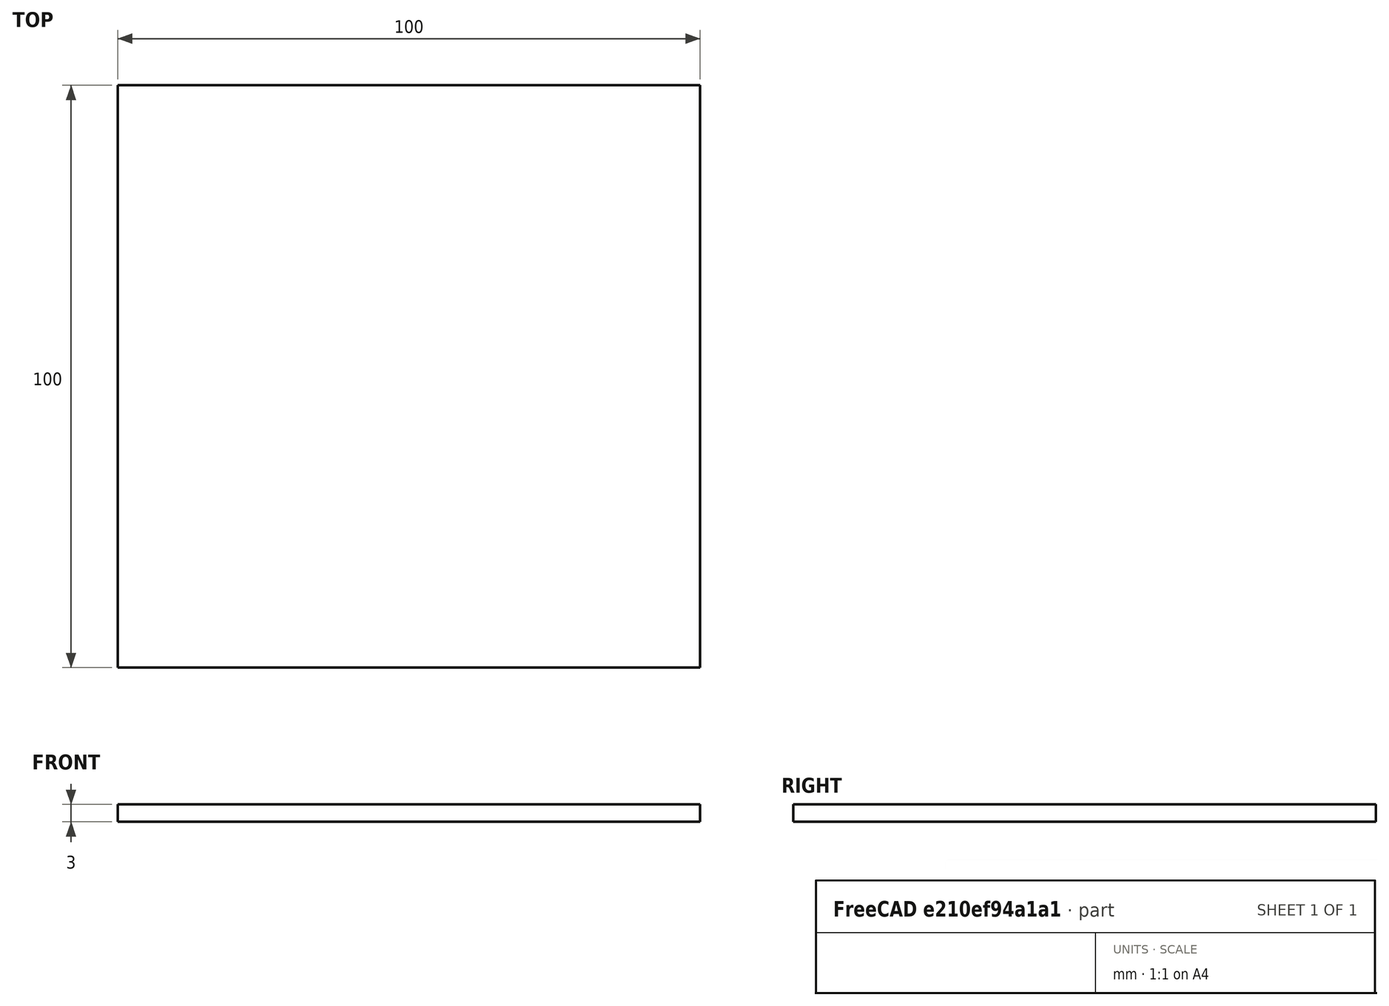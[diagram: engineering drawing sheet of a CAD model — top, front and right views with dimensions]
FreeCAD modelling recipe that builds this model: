
FCSTD DOCUMENT  (FreeCAD 0.15R4671 (Git))
Label: square_plate
License: All rights reserved
LicenseURL: http://en.wikipedia.org/wiki/All_rights_reserved
objects: Sketcher::SketchObject×1, PartDesign::Pad×1
note: 3 computed .brp shape members not serialized (recipe doc carries the construction recipe); baked Part::Feature solids carry a one-line shape summary decoded from their .brp

FEATURE [Sketcher::SketchObject] Sketch
  sketch-geometry (5):
    g0: LineSegment StartX=50 StartY=-50 StartZ=0 EndX=50 EndY=50 EndZ=0
    g1: LineSegment StartX=50 StartY=50 StartZ=0 EndX=-50 EndY=50 EndZ=0
    g2: LineSegment StartX=-50 StartY=50 StartZ=0 EndX=-50 EndY=-50 EndZ=0
    g3: LineSegment StartX=-50 StartY=-50 StartZ=0 EndX=50 EndY=-50 EndZ=0
    g4: Circle [constr] CenterX=0 CenterY=0 CenterZ=0 NormalX=0 NormalY=0 NormalZ=1 Radius=70.7107
  constraints (12):
    c: Coincident(g0,g1)
    c: Coincident(g1,g2)
    c: Coincident(g2,g3)
    c: Coincident(g3,g0)
    c: Equal(g0,g1)
    c: Equal(g0,g2)
    c: Equal(g0,g3)
    c: PointOnObject(g0,g4)
    c: PointOnObject(g1,g4)
    c: PointOnObject(g2,g4)
    c: PointOnObject(g3,g4)
    c: Coincident(g1,g-1)
FEATURE [PartDesign::Pad] Pad
  Length = 3
  Length2 = 100
  Sketch = -> Sketch
  Type = 0
